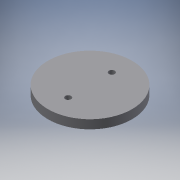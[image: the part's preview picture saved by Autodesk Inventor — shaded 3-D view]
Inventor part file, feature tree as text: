
AUTODESK INVENTOR PART (.ipt)
format: ipt  version: 2016 (Build 200138000, 138)  size: 108,544 bytes
history: native  units: mm
features: extrude x2, sketch x2
ambient origin geometry x8: Origin, YZ Plane, XZ Plane, XY Plane, X Axis, Y Axis, Z Axis, Center Point
bodies: Solid1 (feature_tree)
feature tree (4):
  extrude  "Extrusion1"  Depth=3.0mm TaperAngle=0.0deg
  extrude  "Extrusion4"  Depth=10.0mm
  sketch  "Sketch1"  dims[d0=28.85mm d3=3.0mm d4=0.0mm]
  sketch  "Sketch2"  dims[d22=9.5mm d31=2.0mm d34=15.0mm d35=7.5mm d36=10.0mm d37=0.0mm]
